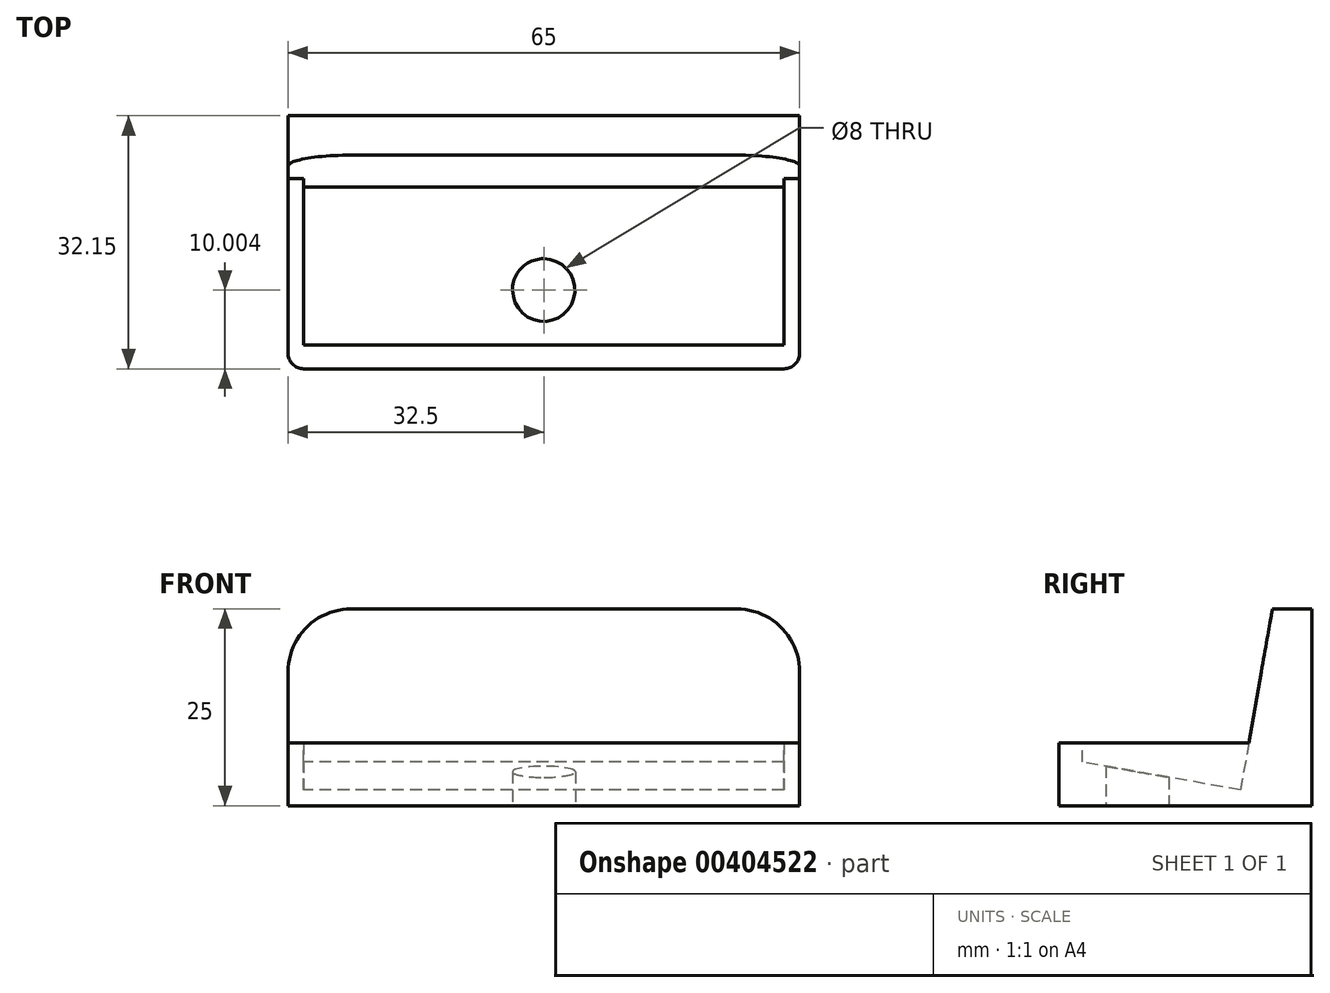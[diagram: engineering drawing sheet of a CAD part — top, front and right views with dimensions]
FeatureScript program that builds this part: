
annotation { "Feature Type Name" : "Feature", "Feature Type Description" : "" }
export const myFeature = defineFeature(function(context is Context, id is Id, definition is map)
    precondition{}
    {
        {
            var Q0;
            Q0=qCreatedBy(makeId("Right.planeOp"),FACE);
            var sketch = newSketch(context, id + "F0", { "sketchPlane" : qUnion([Q0])});
            skLineSegment(sketch, "E0", {"start": v(-32.15, 0) * mm, "end": v(0, 0) * mm});
            skLineSegment(sketch, "E1", {"start": v(0, 0) * mm, "end": v(0, 25) * mm});
            skLineSegment(sketch, "E2", {"start": v(0, 25) * mm, "end": v(-5, 25) * mm});
            skLineSegment(sketch, "E3", {"start": v(-5, 25) * mm, "end": v(-9.06, 2) * mm});
            skLineSegment(sketch, "E4", {"start": v(-9.06, 2) * mm, "end": v(-29.15, 5.54) * mm});
            skLineSegment(sketch, "E5", {"start": v(-29.15, 5.54) * mm, "end": v(-29.15, 8) * mm});
            skLineSegment(sketch, "E6", {"start": v(-29.15, 8) * mm, "end": v(-32.15, 8) * mm});
            skLineSegment(sketch, "E7", {"start": v(-32.15, 8) * mm, "end": v(-32.15, 0) * mm});
            skSolve(sketch);
        }
        {
            var Q0;
            Q0=makeQuery(id+"F0.imprint","IMPRINT",FACE,{"disambiguationData":[TD([[makeQuery(id+"F0.imprint","IMPRINT",EDGE,{"derivedFrom":sQuery(id+"F0.wireOp",EDGE,"E0")}),1.0]])]});
            extrude(context, id + "F1", {"entities" : qUnion([Q0]), "depth" : 32.5 * mm});
        }
        {
            var Q0;
            Q0=makeQuery(id+"F1.opExtrude","CAP_FACE",FACE,{"disambiguationData":[OSD([sQuery(id+"F0.wireOp",EDGE,"E0"),sQuery(id+"F0.wireOp",EDGE,"E1"),sQuery(id+"F0.wireOp",EDGE,"E2"),sQuery(id+"F0.wireOp",EDGE,"E3"),sQuery(id+"F0.wireOp",EDGE,"E4"),sQuery(id+"F0.wireOp",EDGE,"E5"),sQuery(id+"F0.wireOp",EDGE,"E6"),sQuery(id+"F0.wireOp",EDGE,"E7")])],"isStart":false});
            var sketch = newSketch(context, id + "F2", { "sketchPlane" : qUnion([Q0])});
            skLineSegment(sketch, "E8", {"start": v(-29.15, 8) * mm, "end": v(-8, 8) * mm});
            skLineSegment(sketch, "E9", {"start": v(-8, 8) * mm, "end": v(-9.06, 2) * mm});
            skLineSegment(sketch, "E10", {"start": v(-9.06, 2) * mm, "end": v(-29.15, 5.54) * mm});
            skLineSegment(sketch, "E11", {"start": v(-29.15, 5.54) * mm, "end": v(-29.15, 8) * mm});
            skSolve(sketch);
        }
        {
            var Q0;
            Q0=makeQuery(id+"F2.imprint","IMPRINT",FACE,{"disambiguationData":[TD([[makeQuery(id+"F2.imprint","IMPRINT",EDGE,{"derivedFrom":sQuery(id+"F2.wireOp",EDGE,"E8")}),-1.0]])]});
            extrude(context, id + "F3", {"entities" : qUnion([Q0]), "operationType" : NewBodyOperationType.ADD, "oppositeDirection" : true, "depth" : 2 * mm});
        }
        {
            var Q0;
            Q0=makeQuery(id+"F3.opExtrude","SWEPT_EDGE",EDGE,{"disambiguationData":[OSD([sQuery(id+"F0.wireOp",EDGE,"E3"),sQuery(id+"F2.wireOp",EDGE,"E8"),sQuery(id+"F2.wireOp",EDGE,"E9")])]});
            var Q1;
            Q1=makeQuery(id+"F1.opExtrude","CAP_EDGE",EDGE,{"disambiguationData":[OSD([sQuery(id+"F0.wireOp",EDGE,"E2")])],"isStart":false});
            fillet(context, id + "F4", {"entities" : qUnion([Q0, Q1]), "radius" : 8 * mm, "tangentPropagation" : true, "allowEdgeOverflow" : false});
        }
        {
            var Q0;
            Q0=makeQuery(id+"F1.opExtrude","CAP_EDGE",EDGE,{"disambiguationData":[OSD([sQuery(id+"F0.wireOp",EDGE,"E7")])],"isStart":false});
            fillet(context, id + "F5", {"entities" : qUnion([Q0]), "radius" : 2 * mm, "tangentPropagation" : true, "allowEdgeOverflow" : false});
        }
        {
            var Q0;
            Q0=makeQuery(id+"F1.opExtrude","SWEPT_BODY",BODY,{"disambiguationData":[OSD([sQuery(id+"F0.wireOp",EDGE,"E0"),sQuery(id+"F0.wireOp",EDGE,"E1"),sQuery(id+"F0.wireOp",EDGE,"E2"),sQuery(id+"F0.wireOp",EDGE,"E3"),sQuery(id+"F0.wireOp",EDGE,"E4"),sQuery(id+"F0.wireOp",EDGE,"E5"),sQuery(id+"F0.wireOp",EDGE,"E6"),sQuery(id+"F0.wireOp",EDGE,"E7")])]});
            var Q1;
            Q1=qCreatedBy(makeId("Right.planeOp"),FACE);
            mirror(context, id + "F6", {"operationType" : NewBodyOperationType.ADD, "entities" : qUnion([Q0]), "mirrorPlane" : qUnion([Q1])});
        }
        {
            var Q0;
            {var subQ0=makeQuery(id+"F1.opExtrude","SWEPT_FACE",FACE,{"disambiguationData":[OSD([sQuery(id+"F0.wireOp",EDGE,"E0")])]});Q0=makeQuery(id+"F6.boolean.opBoolean","MERGE",FACE,{"derivedFrom":[subQ0,makeQuery(id+"F6.opPattern","COPY",FACE,{"derivedFrom":subQ0,"instanceName":"1"})]});}
            var sketch = newSketch(context, id + "F7", { "sketchPlane" : qUnion([Q0])});
            skCircle(sketch, "E12", {"center": v(0, 22.15) * mm, "radius": 4 * mm});
            skSolve(sketch);
        }
        {
            var Q0;
            Q0=makeQuery(id+"F7.imprint","IMPRINT",FACE,{"disambiguationData":[TD([[makeQuery(id+"F7.imprint","IMPRINT",EDGE,{"derivedFrom":sQuery(id+"F7.wireOp",EDGE,"E12")}),1.0]])]});
            extrude(context, id + "F8", {"entities" : qUnion([Q0]), "operationType" : NewBodyOperationType.REMOVE, "endBound" : BoundingType.UP_TO_NEXT, "oppositeDirection" : true, "depth" : 25 * mm});
        }
    });
